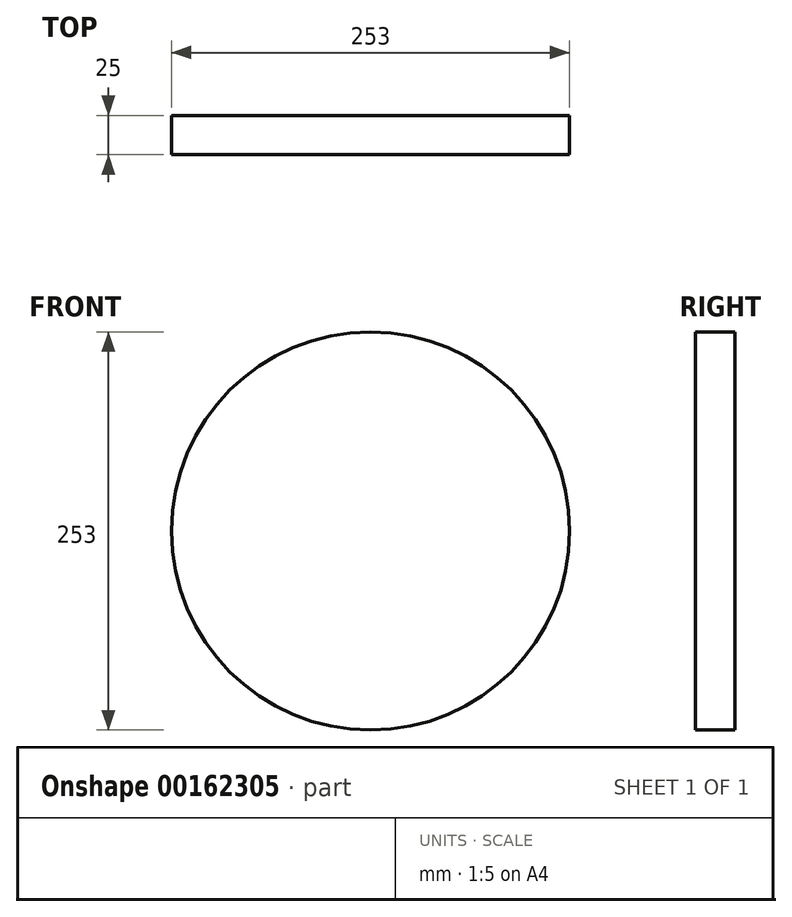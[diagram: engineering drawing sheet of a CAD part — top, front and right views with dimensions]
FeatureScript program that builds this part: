
annotation { "Feature Type Name" : "Feature", "Feature Type Description" : "" }
export const myFeature = defineFeature(function(context is Context, id is Id, definition is map)
    precondition{}
    {
        {
            var Q0;
            Q0=qCreatedBy(makeId("Front.planeOp"),FACE);
            var sketch = newSketch(context, id + "F0", { "sketchPlane" : qUnion([Q0])});
            skCircle(sketch, "E0", {"center": v(0, 0) * mm, "radius": 126.5 * mm});
            skSolve(sketch);
        }
        {
            var Q0;
            Q0=qSketchRegion(id+"F0",true);
            extrude(context, id + "F1", {"entities" : qUnion([Q0]), "depth" : 25 * mm});
        }
    });
